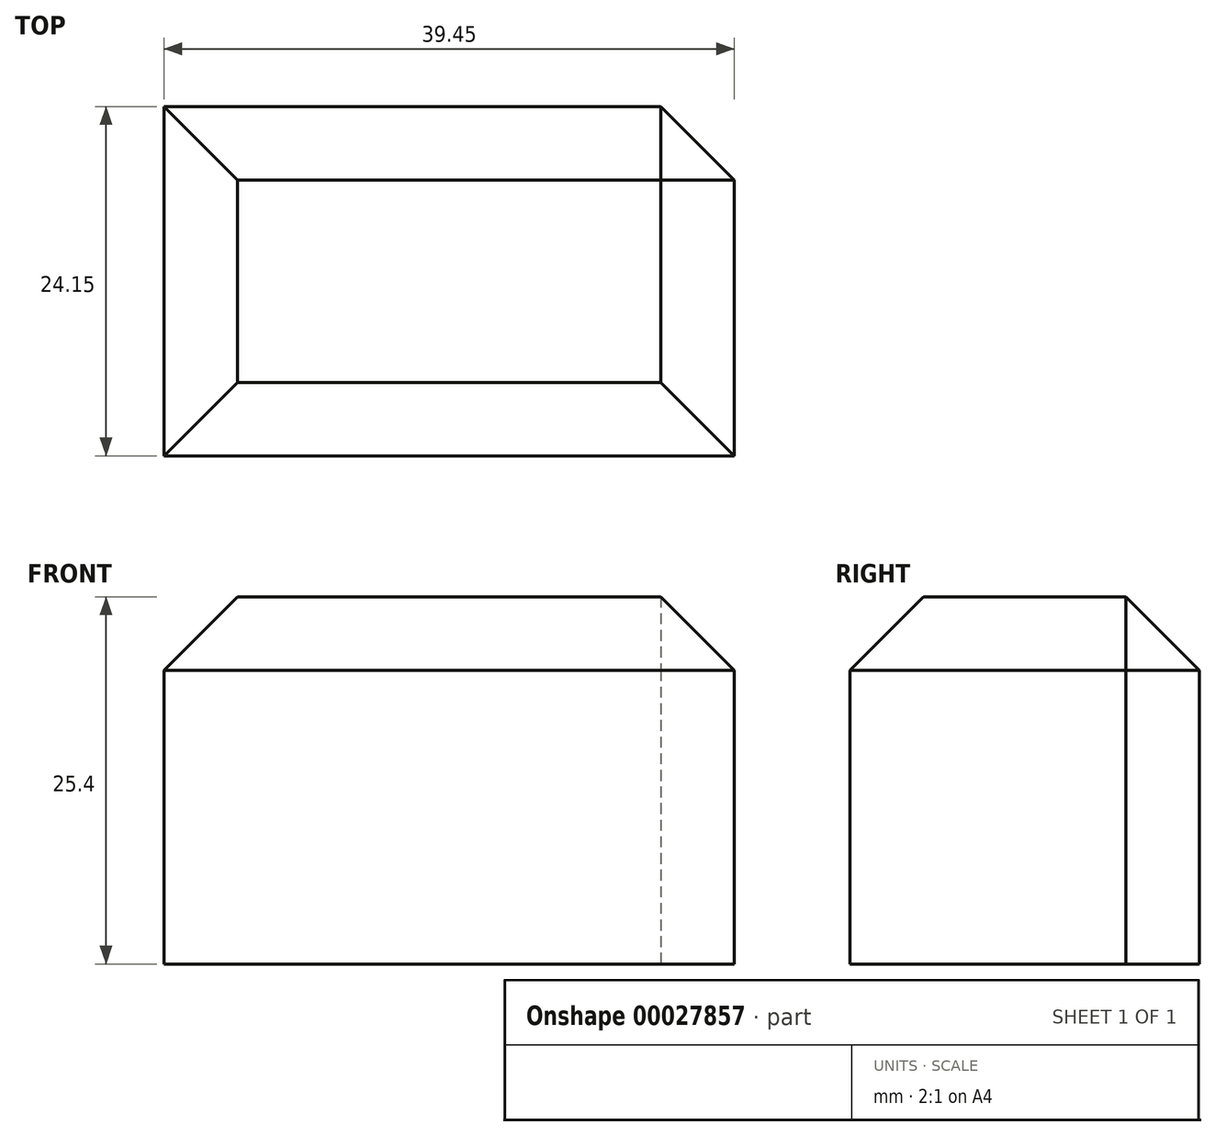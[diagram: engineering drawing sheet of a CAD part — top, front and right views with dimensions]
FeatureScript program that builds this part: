
annotation { "Feature Type Name" : "Feature", "Feature Type Description" : "" }
export const myFeature = defineFeature(function(context is Context, id is Id, definition is map)
    precondition{}
    {
        {
            var Q0;
            Q0=qCreatedBy(makeId("Top.planeOp"),FACE);
            var sketch = newSketch(context, id + "F0", { "sketchPlane" : qUnion([Q0])});
            skLineSegment(sketch, "E0.bottom", {"start": v(-26.05, 28.33) * mm, "end": v(30.9, 28.33) * mm});
            skLineSegment(sketch, "E0.top", {"start": v(-26.05, -23.48) * mm, "end": v(30.9, -23.48) * mm});
            skLineSegment(sketch, "E0.left", {"start": v(-26.05, 28.33) * mm, "end": v(-26.05, -23.48) * mm});
            skLineSegment(sketch, "E0.right", {"start": v(30.9, 28.33) * mm, "end": v(30.9, -23.48) * mm});
            skLineSegment(sketch, "E1.bottom", {"start": v(-17.71, 14.77) * mm, "end": v(21.74, 14.77) * mm});
            skLineSegment(sketch, "E1.top", {"start": v(-17.71, -9.38) * mm, "end": v(21.74, -9.38) * mm});
            skLineSegment(sketch, "E1.left", {"start": v(-17.71, 14.77) * mm, "end": v(-17.71, -9.38) * mm});
            skLineSegment(sketch, "E1.right", {"start": v(21.74, 14.77) * mm, "end": v(21.74, -9.38) * mm});
            skSolve(sketch);
        }
        {
            var Q0;
            Q0=makeQuery(id+"F0.imprint","IMPRINT",FACE,{"disambiguationData":[TD([[makeQuery(id+"F0.imprint","IMPRINT",EDGE,{"derivedFrom":sQuery(id+"F0.wireOp",EDGE,"E1.bottom")}),-1.0]])]});
            extrude(context, id + "F1", {"entities" : qUnion([Q0]), "depth" : 25.4 * mm});
        }
        {
            var Q0;
            Q0=makeQuery(id+"F1.opExtrude","CAP_EDGE",EDGE,{"disambiguationData":[OSD([sQuery(id+"F0.wireOp",EDGE,"E1.bottom")])],"isStart":false});
            var Q1;
            Q1=makeQuery(id+"F1.opExtrude","CAP_EDGE",EDGE,{"disambiguationData":[OSD([sQuery(id+"F0.wireOp",EDGE,"E1.left")])],"isStart":false});
            var Q2;
            Q2=makeQuery(id+"F1.opExtrude","CAP_EDGE",EDGE,{"disambiguationData":[OSD([sQuery(id+"F0.wireOp",EDGE,"E1.right")])],"isStart":false});
            var Q3;
            Q3=makeQuery(id+"F1.opExtrude","CAP_EDGE",EDGE,{"disambiguationData":[OSD([sQuery(id+"F0.wireOp",EDGE,"E1.top")])],"isStart":false});
            var Q4;
            Q4=makeQuery(id+"F1.opExtrude","SWEPT_EDGE",EDGE,{"disambiguationData":[OSD([sQuery(id+"F0.wireOp",EDGE,"E1.bottom"),sQuery(id+"F0.wireOp",EDGE,"E1.right")])]});
            chamfer(context, id + "F2", {"entities" : qUnion([Q0, Q1, Q2, Q3, Q4]), "width" : 5.08 * mm, "tangentPropagation" : true});
        }
    });
